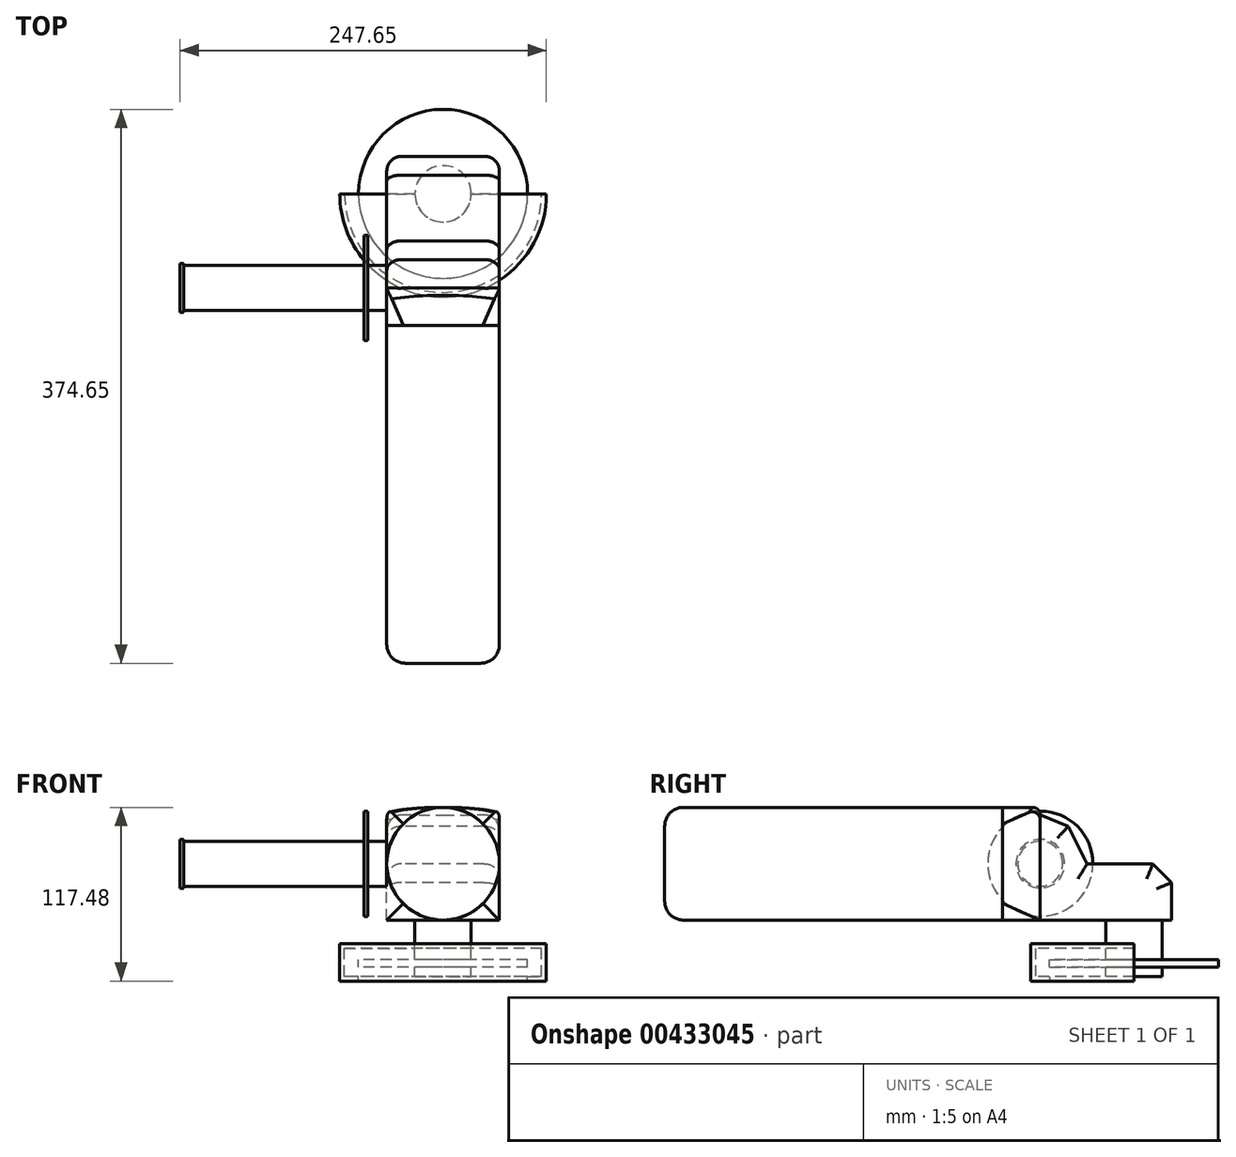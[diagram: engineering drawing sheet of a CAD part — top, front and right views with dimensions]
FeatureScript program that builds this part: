
annotation { "Feature Type Name" : "Feature", "Feature Type Description" : "" }
export const myFeature = defineFeature(function(context is Context, id is Id, definition is map)
    precondition{}
    {
        {
            var Q0;
            Q0=qCreatedBy(makeId("Front.planeOp"),FACE);
            var sketch = newSketch(context, id + "F0", { "sketchPlane" : qUnion([Q0])});
            skCircle(sketch, "E0", {"center": v(0, 0) * mm, "radius": 38.1 * mm});
            skSolve(sketch);
        }
        {
            var Q0;
            Q0=makeQuery(id+"F0.imprint","IMPRINT",FACE,{"disambiguationData":[TD([[makeQuery(id+"F0.imprint","IMPRINT",EDGE,{"derivedFrom":sQuery(id+"F0.wireOp",EDGE,"E0")}),1.0]])]});
            extrude(context, id + "F1", {"entities" : qUnion([Q0]), "depth" : 228.6 * mm});
        }
        {
            var Q0;
            Q0=qCreatedBy(makeId("Front.planeOp"),FACE);
            cPlane(context, id + "F2", {"entities" : qUnion([Q0]), "cplaneType" : CPlaneType.OFFSET, "offset" : 25.4 * mm, "oppositeDirection" : true, "width" : 152.4 * mm, "height" : 152.4 * mm});
        }
        {
            var Q0;
            Q0=qCreatedBy(id+"F2.planeOp",FACE);
            var sketch = newSketch(context, id + "F3", { "sketchPlane" : qUnion([Q0])});
            skLineSegment(sketch, "E1.bottom", {"start": v(38.1, 38.1) * mm, "end": v(-38.1, 38.1) * mm});
            skLineSegment(sketch, "E1.top", {"start": v(38.1, -38.1) * mm, "end": v(-38.1, -38.1) * mm});
            skLineSegment(sketch, "E1.left", {"start": v(38.1, 38.1) * mm, "end": v(38.1, -38.1) * mm});
            skLineSegment(sketch, "E1.right", {"start": v(-38.1, 38.1) * mm, "end": v(-38.1, -38.1) * mm});
            skSolve(sketch);
        }
        {
            var Q0;
            Q0=makeQuery(id+"F1.opExtrude","CAP_FACE",FACE,{"disambiguationData":[OSD([sQuery(id+"F0.wireOp",EDGE,"E0")])],"isStart":true});
            var Q1;
            Q1=makeQuery(id+"F3.imprint","IMPRINT",FACE,{"disambiguationData":[TD([[makeQuery(id+"F3.imprint","IMPRINT",EDGE,{"derivedFrom":sQuery(id+"F3.wireOp",EDGE,"E1.bottom")}),1.0]])]});
            loft(context, id + "F4", {"operationType" : NewBodyOperationType.ADD, "sheetProfilesArray" : [{ "sheetProfileEntities" : qUnion([Q0]) }, { "sheetProfileEntities" : qUnion([Q1]) }]});
        }
        {
            var Q0;
            Q0=qCreatedBy(makeId("Right.planeOp"),FACE);
            cPlane(context, id + "F5", {"entities" : qUnion([Q0]), "cplaneType" : CPlaneType.OFFSET, "offset" : 38.1 * mm, "oppositeDirection" : true, "width" : 152.4 * mm, "height" : 152.4 * mm});
        }
        {
            var Q0;
            Q0=qCreatedBy(id+"F5.planeOp",FACE);
            var sketch = newSketch(context, id + "F6", { "sketchPlane" : qUnion([Q0])});
            skLineSegment(sketch, "E2", {"start": v(25.4, -38.1) * mm, "end": v(114.3, -38.1) * mm});
            skLineSegment(sketch, "E3", {"start": v(114.3, -38.1) * mm, "end": v(114.3, -12.7) * mm});
            skLineSegment(sketch, "E4", {"start": v(114.3, -12.7) * mm, "end": v(101.6, 0) * mm});
            skLineSegment(sketch, "E5", {"start": v(101.6, 0) * mm, "end": v(57.15, 0) * mm});
            skLineSegment(sketch, "E6", {"start": v(57.15, 0) * mm, "end": v(44.45, 25.4) * mm});
            skLineSegment(sketch, "E7", {"start": v(44.45, 25.4) * mm, "end": v(25.4, 33.02) * mm});
            skLineSegment(sketch, "E8", {"start": v(25.4, 33.02) * mm, "end": v(25.4, -38.1) * mm});
            skSolve(sketch);
        }
        {
            var Q0;
            Q0=makeQuery(id+"F6.imprint","IMPRINT",FACE,{"disambiguationData":[TD([[makeQuery(id+"F6.imprint","IMPRINT",EDGE,{"derivedFrom":sQuery(id+"F6.wireOp",EDGE,"E2")}),1.0]])]});
            extrude(context, id + "F7", {"entities" : qUnion([Q0]), "operationType" : NewBodyOperationType.ADD, "depth" : 76.2 * mm});
        }
        {
            var Q0;
            Q0=makeQuery(id+"F7.opExtrude","CAP_EDGE",EDGE,{"disambiguationData":[OSD([sQuery(id+"F6.wireOp",EDGE,"E5")])],"isStart":true});
            var Q1;
            Q1=makeQuery(id+"F7.opExtrude","CAP_EDGE",EDGE,{"disambiguationData":[OSD([sQuery(id+"F6.wireOp",EDGE,"E4")])],"isStart":true});
            var Q2;
            Q2=makeQuery(id+"F7.opExtrude","CAP_EDGE",EDGE,{"disambiguationData":[OSD([sQuery(id+"F6.wireOp",EDGE,"E3")])],"isStart":true});
            var Q3;
            Q3=makeQuery(id+"F7.opExtrude","CAP_EDGE",EDGE,{"disambiguationData":[OSD([sQuery(id+"F6.wireOp",EDGE,"E3")])],"isStart":false});
            var Q4;
            Q4=makeQuery(id+"F7.opExtrude","CAP_EDGE",EDGE,{"disambiguationData":[OSD([sQuery(id+"F6.wireOp",EDGE,"E4")])],"isStart":false});
            var Q5;
            Q5=makeQuery(id+"F7.opExtrude","CAP_EDGE",EDGE,{"disambiguationData":[OSD([sQuery(id+"F6.wireOp",EDGE,"E5")])],"isStart":false});
            var Q6;
            Q6=makeQuery(id+"F7.opExtrude","CAP_EDGE",EDGE,{"disambiguationData":[OSD([sQuery(id+"F6.wireOp",EDGE,"E6")])],"isStart":false});
            var Q7;
            Q7=makeQuery(id+"F7.opExtrude","CAP_EDGE",EDGE,{"disambiguationData":[OSD([sQuery(id+"F6.wireOp",EDGE,"E7")])],"isStart":false});
            var Q8;
            Q8=makeQuery(id+"F7.opExtrude","CAP_EDGE",EDGE,{"disambiguationData":[OSD([sQuery(id+"F6.wireOp",EDGE,"E7")])],"isStart":true});
            var Q9;
            Q9=makeQuery(id+"F7.opExtrude","CAP_EDGE",EDGE,{"disambiguationData":[OSD([sQuery(id+"F6.wireOp",EDGE,"E6")])],"isStart":true});
            fillet(context, id + "F8", {"entities" : qUnion([Q0, Q1, Q2, Q3, Q4, Q5, Q6, Q7, Q8, Q9]), "radius" : 10.16 * mm, "tangentPropagation" : true, "allowEdgeOverflow" : false});
        }
        {
            var Q0;
            Q0=makeQuery(id+"F4.opLoft","MID_CAP_EDGE",EDGE,{"disambiguationData":[OSD([sQuery(id+"F3.wireOp",EDGE,"E1.bottom"),sQuery(id+"F3.wireOp",EDGE,"E1.left"),sQuery(id+"F3.wireOp",EDGE,"E1.right")])],"capPos":1.0});
            fillet(context, id + "F9", {"entities" : qUnion([Q0]), "radius" : 5.08 * mm, "tangentPropagation" : true, "allowEdgeOverflow" : false});
        }
        {
            var Q0;
            Q0=makeQuery(id+"F1.opExtrude","CAP_EDGE",EDGE,{"disambiguationData":[OSD([sQuery(id+"F0.wireOp",EDGE,"E0")])],"isStart":false});
            fillet(context, id + "F10", {"entities" : qUnion([Q0]), "radius" : 12.7 * mm, "tangentPropagation" : true, "allowEdgeOverflow" : false});
        }
        {
            var Q0;
            Q0=makeQuery(id+"F7.opExtrude","SWEPT_FACE",FACE,{"disambiguationData":[OSD([sQuery(id+"F6.wireOp",EDGE,"E2")])]});
            var sketch = newSketch(context, id + "F11", { "sketchPlane" : qUnion([Q0])});
            skSolve(sketch);
        }
        {
            var Q0;
            {var subQ0=sQuery(id+"F6.wireOp",EDGE,"E2");Q0=makeQuery(id+"F11.imprint","IMPRINT",FACE,{"disambiguationData":[TD([[makeQuery(id+"F11.imprint","IMPRINT",EDGE,{"derivedFrom":makeQuery(id+"F7.opExtrude","CAP_EDGE",EDGE,{"disambiguationData":[OSD([subQ0])],"isStart":true})}),1.0]])]});}
            var sketch = newSketch(context, id + "F12", { "sketchPlane" : qUnion([Q0])});
            skCircle(sketch, "E9", {"center": v(0, -88.9) * mm, "radius": 19.05 * mm});
            skSolve(sketch);
        }
        {
            var Q0;
            Q0=makeQuery(id+"F12.imprint","IMPRINT",FACE,{"disambiguationData":[TD([[makeQuery(id+"F12.imprint","IMPRINT",EDGE,{"derivedFrom":sQuery(id+"F12.wireOp",EDGE,"E9")}),1.0]])]});
            extrude(context, id + "F13", {"entities" : qUnion([Q0]), "operationType" : NewBodyOperationType.ADD, "depth" : 38.1 * mm});
        }
        {
            var Q0;
            Q0=makeQuery(id+"F7.opExtrude","SWEPT_FACE",FACE,{"disambiguationData":[OSD([sQuery(id+"F6.wireOp",EDGE,"E3")])]});
            cPlane(context, id + "F14", {"entities" : qUnion([Q0]), "cplaneType" : CPlaneType.OFFSET, "offset" : 25.4 * mm, "oppositeDirection" : true, "width" : 152.4 * mm, "height" : 152.4 * mm});
        }
        {
            var Q0;
            Q0=qCreatedBy(id+"F14.planeOp",FACE);
            var sketch = newSketch(context, id + "F15", { "sketchPlane" : qUnion([Q0])});
            skLineSegment(sketch, "E10", {"start": v(0, 56.85) * mm, "end": v(0, -87.91) * mm});
            skLineSegment(sketch, "E11", {"start": v(19.05, -53.98) * mm, "end": v(69.85, -53.97) * mm});
            skLineSegment(sketch, "E12", {"start": v(69.85, -53.97) * mm, "end": v(69.85, -79.38) * mm});
            skLineSegment(sketch, "E13", {"start": v(69.85, -79.38) * mm, "end": v(57.15, -79.38) * mm});
            skLineSegment(sketch, "E14", {"start": v(57.15, -79.38) * mm, "end": v(57.15, -76.2) * mm});
            skLineSegment(sketch, "E15", {"start": v(57.15, -76.2) * mm, "end": v(66.68, -76.2) * mm});
            skLineSegment(sketch, "E16", {"start": v(66.68, -76.2) * mm, "end": v(66.68, -57.15) * mm});
            skLineSegment(sketch, "E17", {"start": v(66.68, -57.15) * mm, "end": v(19.05, -57.15) * mm});
            skLineSegment(sketch, "E18", {"start": v(19.05, -57.15) * mm, "end": v(19.05, -53.98) * mm});
            skLineSegment(sketch, "E19", {"start": v(19.05, -64.77) * mm, "end": v(57.15, -64.77) * mm});
            skLineSegment(sketch, "E20", {"start": v(57.15, -64.77) * mm, "end": v(57.15, -69.85) * mm});
            skLineSegment(sketch, "E21", {"start": v(57.15, -69.85) * mm, "end": v(19.05, -69.85) * mm});
            skLineSegment(sketch, "E22", {"start": v(19.05, -69.85) * mm, "end": v(19.05, -64.77) * mm});
            skSolve(sketch);
        }
        {
            var Q0;
            Q0=makeQuery(id+"F15.imprint","IMPRINT",FACE,{"disambiguationData":[TD([[makeQuery(id+"F15.imprint","IMPRINT",EDGE,{"derivedFrom":sQuery(id+"F15.wireOp",EDGE,"E11")}),-1.0]])]});
            var Q1;
            Q1=sQuery(id+"F15.wireOp",EDGE,"E10");
            revolve(context, id + "F16", {"operationType" : NewBodyOperationType.ADD, "entities" : qUnion([Q0]), "axis" : qUnion([Q1]), "revolveType" : RevolveType.ONE_DIRECTION, "oppositeDirection" : true, "angle" : 180 * degree});
        }
        {
            var Q0;
            Q0=makeQuery(id+"F15.imprint","IMPRINT",FACE,{"disambiguationData":[TD([[makeQuery(id+"F15.imprint","IMPRINT",EDGE,{"derivedFrom":sQuery(id+"F15.wireOp",EDGE,"E19")}),-1.0]])]});
            var Q1;
            Q1=sQuery(id+"F15.wireOp",EDGE,"E10");
            revolve(context, id + "F17", {"operationType" : NewBodyOperationType.ADD, "entities" : qUnion([Q0]), "axis" : qUnion([Q1]), "revolveType" : RevolveType.FULL});
        }
        {
            var Q0;
            Q0=qCreatedBy(id+"F2.planeOp",FACE);
            var sketch = newSketch(context, id + "F18", { "sketchPlane" : qUnion([Q0])});
            skLineSegment(sketch, "E23", {"start": v(-38.1, 0) * mm, "end": v(-38.1, 15.24) * mm});
            skLineSegment(sketch, "E24", {"start": v(-38.1, 15.24) * mm, "end": v(-50.8, 15.24) * mm});
            skLineSegment(sketch, "E25", {"start": v(-50.8, 15.24) * mm, "end": v(-50.8, 35.56) * mm});
            skLineSegment(sketch, "E26", {"start": v(-50.8, 35.56) * mm, "end": v(-53.34, 35.56) * mm});
            skLineSegment(sketch, "E27", {"start": v(-53.34, 35.56) * mm, "end": v(-53.34, 15.24) * mm});
            skLineSegment(sketch, "E28", {"start": v(-53.34, 15.24) * mm, "end": v(-175.26, 15.24) * mm});
            skLineSegment(sketch, "E29", {"start": v(-175.26, 15.24) * mm, "end": v(-175.26, 16.5) * mm});
            skLineSegment(sketch, "E30", {"start": v(-175.26, 16.5) * mm, "end": v(-177.8, 16.5) * mm});
            skLineSegment(sketch, "E31", {"start": v(-177.8, 16.5) * mm, "end": v(-177.8, 0) * mm});
            skLineSegment(sketch, "E32", {"start": v(-177.8, 0) * mm, "end": v(-38.1, 0) * mm, "construction": true});
            skLineSegment(sketch, "E33", {"start": v(-177.8, 0) * mm, "end": v(-38.1, 0) * mm});
            skSolve(sketch);
        }
        {
            var Q0;
            Q0=makeQuery(id+"F18.imprint","IMPRINT",FACE,{"disambiguationData":[TD([[makeQuery(id+"F18.imprint","IMPRINT",EDGE,{"derivedFrom":sQuery(id+"F18.wireOp",EDGE,"E23")}),1.0]])]});
            var Q1;
            Q1=sQuery(id+"F18.wireOp",EDGE,"E33");
            revolve(context, id + "F19", {"entities" : qUnion([Q0]), "axis" : qUnion([Q1]), "revolveType" : RevolveType.FULL});
        }
    });
